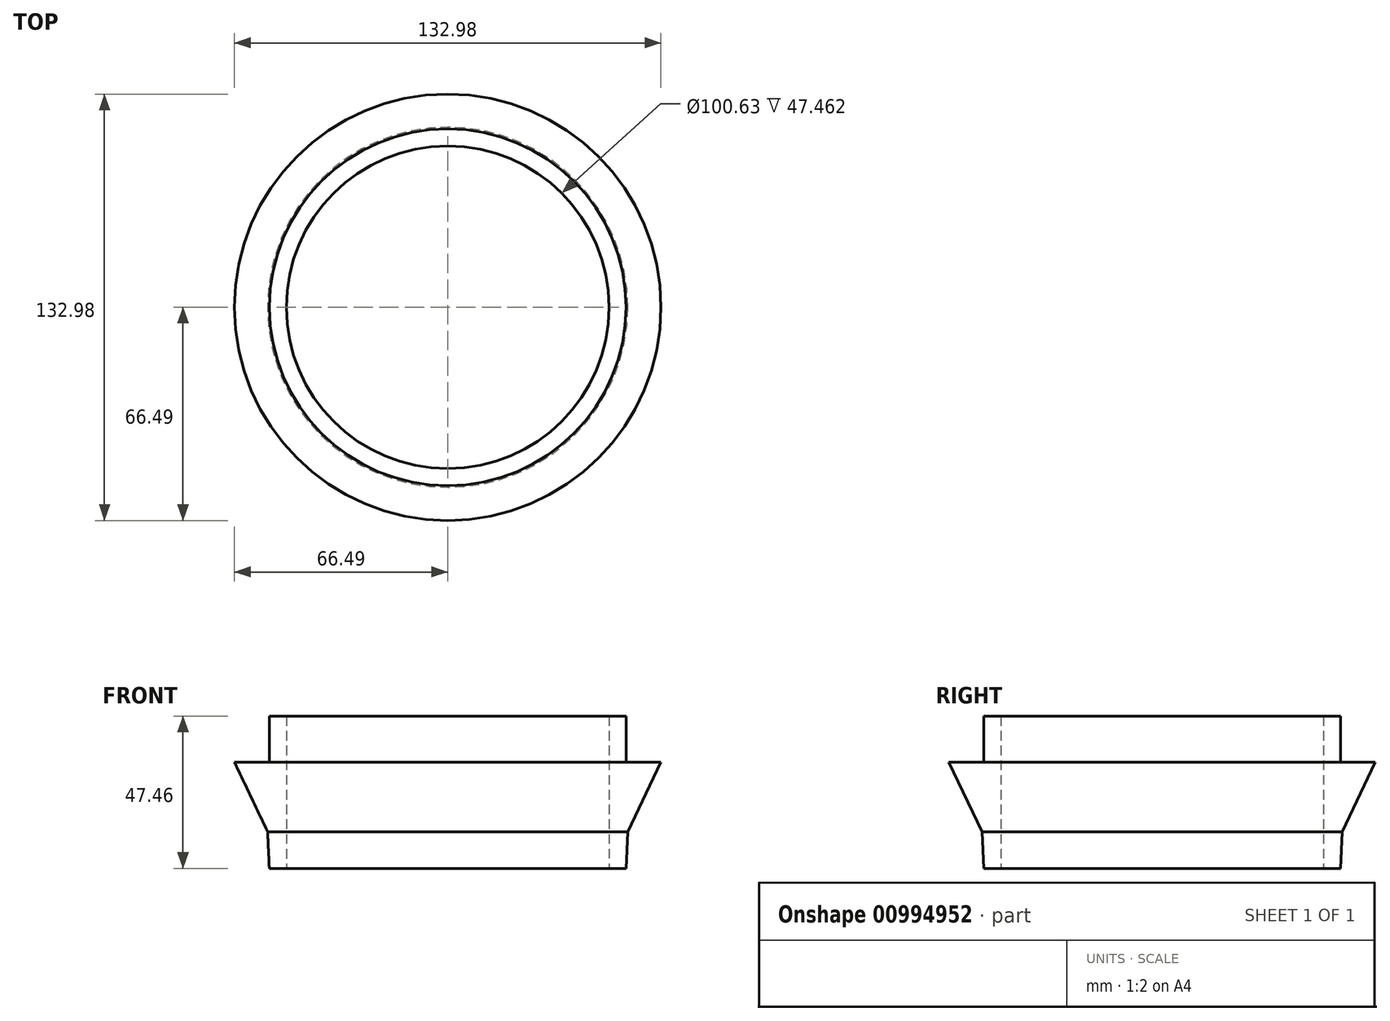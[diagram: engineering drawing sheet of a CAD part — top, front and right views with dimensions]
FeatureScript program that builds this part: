
annotation { "Feature Type Name" : "Feature", "Feature Type Description" : "" }
export const myFeature = defineFeature(function(context is Context, id is Id, definition is map)
    precondition{}
    {
        {
            var Q0;
            Q0=qCreatedBy(makeId("Front.planeOp"),FACE);
            var sketch = newSketch(context, id + "F0", { "sketchPlane" : qUnion([Q0])});
            skLineSegment(sketch, "E0", {"start": v(-56.15, 23.4) * mm, "end": v(-66.49, 45.14) * mm});
            skLineSegment(sketch, "E1", {"start": v(-66.49, 45.14) * mm, "end": v(-55.62, 45.14) * mm});
            skLineSegment(sketch, "E2", {"start": v(-55.62, 45.14) * mm, "end": v(-55.62, 59.46) * mm});
            skLineSegment(sketch, "E3", {"start": v(-55.62, 59.46) * mm, "end": v(-50.31, 59.46) * mm});
            skLineSegment(sketch, "E4", {"start": v(-50.31, 59.46) * mm, "end": v(-50.31, 12) * mm});
            skLineSegment(sketch, "E5", {"start": v(-50.31, 12) * mm, "end": v(-55.62, 12) * mm});
            skLineSegment(sketch, "E6", {"start": v(-55.62, 12) * mm, "end": v(-56.15, 23.4) * mm});
            skLineSegment(sketch, "E7", {"start": v(0, 0) * mm, "end": v(0, 58.13) * mm, "construction": true});
            skSolve(sketch);
        }
        {
            var Q0;
            Q0=makeQuery(id+"F0.imprint","IMPRINT",FACE,{"disambiguationData":[TD([[makeQuery(id+"F0.imprint","IMPRINT",EDGE,{"derivedFrom":sQuery(id+"F0.wireOp",EDGE,"E0")}),-1.0]])]});
            var Q1;
            Q1=sQuery(id+"F0.wireOp",EDGE,"E7");
            revolve(context, id + "F1", {"surfaceOperationType" : NewSurfaceOperationType.NEW, "entities" : qUnion([Q0]), "axis" : qUnion([Q1]), "revolveType" : RevolveType.FULL});
        }
    });
